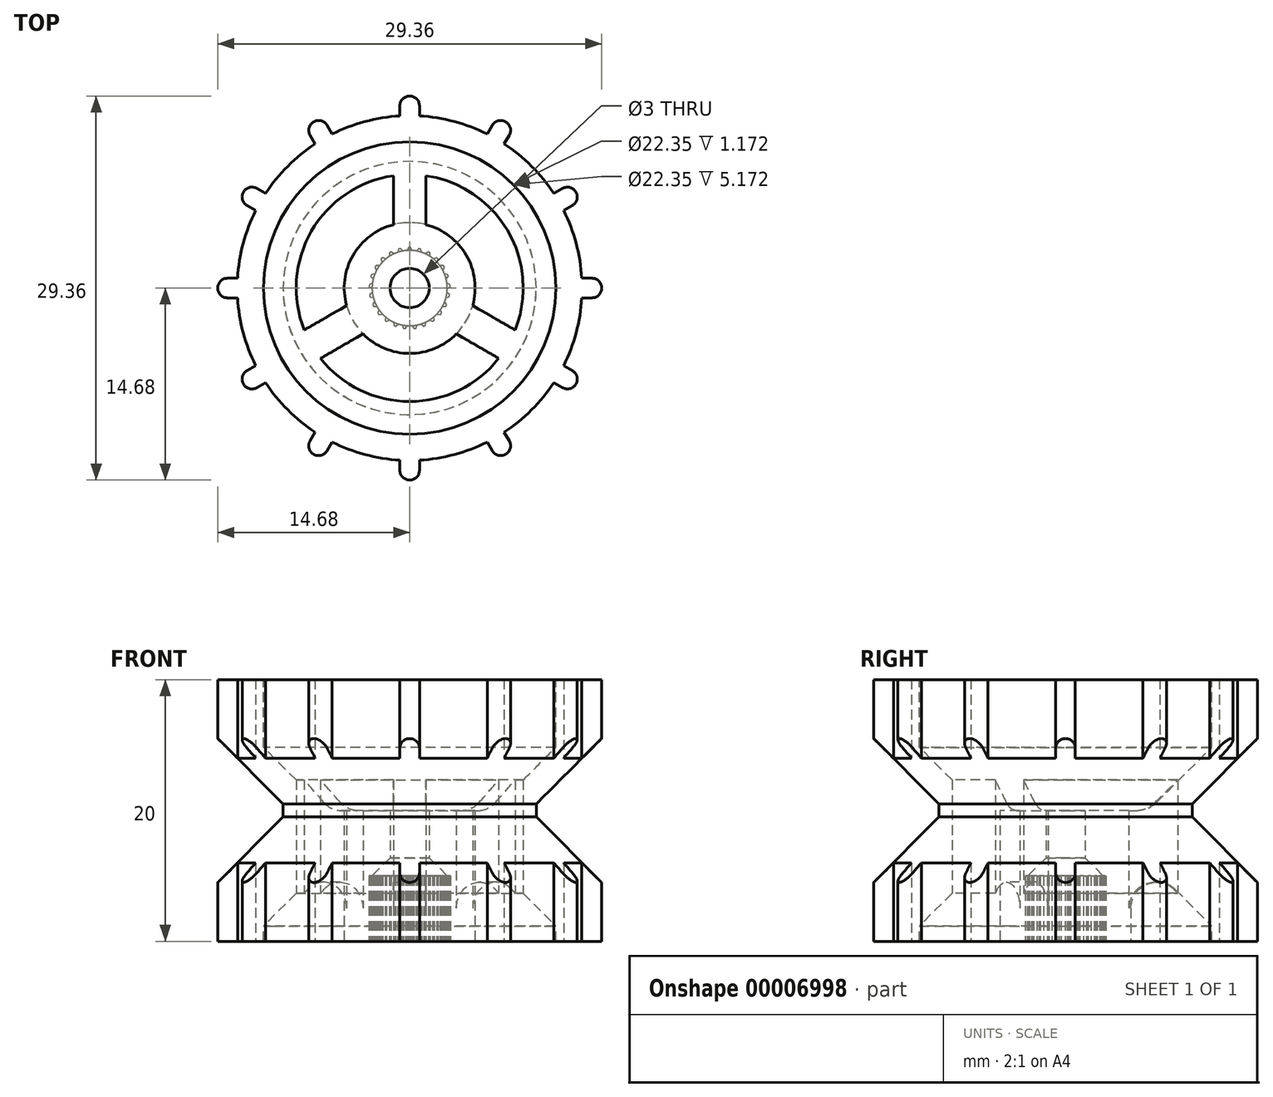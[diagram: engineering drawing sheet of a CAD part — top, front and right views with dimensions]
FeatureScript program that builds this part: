
annotation { "Feature Type Name" : "Feature", "Feature Type Description" : "" }
export const myFeature = defineFeature(function(context is Context, id is Id, definition is map)
    precondition{}
    {
        {
            var Q0;
            Q0=qCreatedBy(makeId("Top.planeOp"),FACE);
            var sketch = newSketch(context, id + "F0", { "sketchPlane" : qUnion([Q0])});
            skLineSegment(sketch, "E0.0", {"start": v(0.07, 3.1) * mm, "end": v(-0.08, 3.1) * mm});
            skLineSegment(sketch, "E0.1", {"start": v(0.25, 2.79) * mm, "end": v(0.07, 3.1) * mm});
            skArc(sketch, "E0.2", {"start": v(0.45, 2.76) * mm, "mid": v(0.35, 2.78) * mm, "end": v(0.25, 2.79) * mm});
            skLineSegment(sketch, "E1.1.0", {"start": v(-0.7, 3.02) * mm, "end": v(-0.84, 2.98) * mm});
            skLineSegment(sketch, "E1.1.1", {"start": v(-0.45, 2.76) * mm, "end": v(-0.7, 3.02) * mm});
            skArc(sketch, "E1.1.2", {"start": v(-0.25, 2.79) * mm, "mid": v(-0.35, 2.78) * mm, "end": v(-0.45, 2.76) * mm});
            skLineSegment(sketch, "E1.2.0", {"start": v(-1.43, 2.75) * mm, "end": v(-1.56, 2.68) * mm});
            skLineSegment(sketch, "E1.2.1", {"start": v(-1.12, 2.56) * mm, "end": v(-1.43, 2.75) * mm});
            skArc(sketch, "E1.2.2", {"start": v(-0.94, 2.64) * mm, "mid": v(-1.03, 2.6) * mm, "end": v(-1.12, 2.56) * mm});
            skLineSegment(sketch, "E1.3.0", {"start": v(-2.07, 2.31) * mm, "end": v(-2.18, 2.2) * mm});
            skLineSegment(sketch, "E1.3.1", {"start": v(-1.73, 2.2) * mm, "end": v(-2.07, 2.31) * mm});
            skArc(sketch, "E1.3.2", {"start": v(-1.56, 2.32) * mm, "mid": v(-1.65, 2.27) * mm, "end": v(-1.73, 2.2) * mm});
            skLineSegment(sketch, "E1.4.0", {"start": v(-2.58, 1.72) * mm, "end": v(-2.66, 1.6) * mm});
            skLineSegment(sketch, "E1.4.1", {"start": v(-2.22, 1.7) * mm, "end": v(-2.58, 1.72) * mm});
            skArc(sketch, "E1.4.2", {"start": v(-2.1, 1.86) * mm, "mid": v(-2.16, 1.78) * mm, "end": v(-2.22, 1.7) * mm});
            skLineSegment(sketch, "E1.5.0", {"start": v(-2.93, 1.03) * mm, "end": v(-2.97, 0.89) * mm});
            skLineSegment(sketch, "E1.5.1", {"start": v(-2.58, 1.1) * mm, "end": v(-2.93, 1.03) * mm});
            skArc(sketch, "E1.5.2", {"start": v(-2.49, 1.28) * mm, "mid": v(-2.53, 1.2) * mm, "end": v(-2.58, 1.1) * mm});
            skLineSegment(sketch, "E1.6.0", {"start": v(-3.09, 0.27) * mm, "end": v(-3.1, 0.12) * mm});
            skLineSegment(sketch, "E1.6.1", {"start": v(-2.77, 0.42) * mm, "end": v(-3.09, 0.27) * mm});
            skArc(sketch, "E1.6.2", {"start": v(-2.73, 0.62) * mm, "mid": v(-2.75, 0.52) * mm, "end": v(-2.77, 0.42) * mm});
            skLineSegment(sketch, "E1.7.0", {"start": v(-3.06, -0.5) * mm, "end": v(-3.03, -0.65) * mm});
            skLineSegment(sketch, "E1.7.1", {"start": v(-2.79, -0.28) * mm, "end": v(-3.06, -0.5) * mm});
            skArc(sketch, "E1.7.2", {"start": v(-2.8, -0.07) * mm, "mid": v(-2.8, -0.18) * mm, "end": v(-2.79, -0.28) * mm});
            skLineSegment(sketch, "E1.8.0", {"start": v(-2.84, -1.25) * mm, "end": v(-2.77, -1.39) * mm});
            skLineSegment(sketch, "E1.8.1", {"start": v(-2.63, -0.96) * mm, "end": v(-2.84, -1.25) * mm});
            skArc(sketch, "E1.8.2", {"start": v(-2.7, -0.77) * mm, "mid": v(-2.66, -0.87) * mm, "end": v(-2.63, -0.96) * mm});
            skLineSegment(sketch, "E1.9.0", {"start": v(-2.44, -1.92) * mm, "end": v(-2.34, -2.03) * mm});
            skLineSegment(sketch, "E1.9.1", {"start": v(-2.3, -1.59) * mm, "end": v(-2.44, -1.92) * mm});
            skArc(sketch, "E1.9.2", {"start": v(-2.42, -1.41) * mm, "mid": v(-2.36, -1.5) * mm, "end": v(-2.3, -1.59) * mm});
            skLineSegment(sketch, "E1.10.0", {"start": v(-1.88, -2.46) * mm, "end": v(-1.76, -2.55) * mm});
            skLineSegment(sketch, "E1.10.1", {"start": v(-1.84, -2.1) * mm, "end": v(-1.88, -2.46) * mm});
            skArc(sketch, "E1.10.2", {"start": v(-1.99, -1.97) * mm, "mid": v(-1.92, -2.04) * mm, "end": v(-1.84, -2.1) * mm});
            skLineSegment(sketch, "E1.11.0", {"start": v(-1.21, -2.85) * mm, "end": v(-1.07, -2.9) * mm});
            skLineSegment(sketch, "E1.11.1", {"start": v(-1.26, -2.5) * mm, "end": v(-1.21, -2.85) * mm});
            skArc(sketch, "E1.11.2", {"start": v(-1.44, -2.4) * mm, "mid": v(-1.35, -2.45) * mm, "end": v(-1.26, -2.5) * mm});
            skLineSegment(sketch, "E1.12.0", {"start": v(-0.46, -3.07) * mm, "end": v(-0.31, -3.08) * mm});
            skLineSegment(sketch, "E1.12.1", {"start": v(-0.6, -2.74) * mm, "end": v(-0.46, -3.07) * mm});
            skArc(sketch, "E1.12.2", {"start": v(-0.8, -2.69) * mm, "mid": v(-0.7, -2.71) * mm, "end": v(-0.6, -2.74) * mm});
            skLineSegment(sketch, "E1.13.0", {"start": v(0.31, -3.08) * mm, "end": v(0.46, -3.07) * mm});
            skLineSegment(sketch, "E1.13.1", {"start": v(0.1, -2.8) * mm, "end": v(0.31, -3.08) * mm});
            skArc(sketch, "E1.13.2", {"start": v(-0.1, -2.8) * mm, "mid": v(0, -2.8) * mm, "end": v(0.1, -2.8) * mm});
            skLineSegment(sketch, "E1.14.0", {"start": v(1.07, -2.9) * mm, "end": v(1.21, -2.85) * mm});
            skLineSegment(sketch, "E1.14.1", {"start": v(0.8, -2.69) * mm, "end": v(1.07, -2.9) * mm});
            skArc(sketch, "E1.14.2", {"start": v(0.6, -2.74) * mm, "mid": v(0.7, -2.71) * mm, "end": v(0.8, -2.69) * mm});
            skLineSegment(sketch, "E1.15.0", {"start": v(1.76, -2.55) * mm, "end": v(1.88, -2.46) * mm});
            skLineSegment(sketch, "E1.15.1", {"start": v(1.44, -2.4) * mm, "end": v(1.76, -2.55) * mm});
            skArc(sketch, "E1.15.2", {"start": v(1.26, -2.5) * mm, "mid": v(1.35, -2.45) * mm, "end": v(1.44, -2.4) * mm});
            skLineSegment(sketch, "E1.16.0", {"start": v(2.34, -2.03) * mm, "end": v(2.44, -1.92) * mm});
            skLineSegment(sketch, "E1.16.1", {"start": v(1.99, -1.97) * mm, "end": v(2.34, -2.03) * mm});
            skArc(sketch, "E1.16.2", {"start": v(1.84, -2.1) * mm, "mid": v(1.92, -2.04) * mm, "end": v(1.99, -1.97) * mm});
            skLineSegment(sketch, "E1.17.0", {"start": v(2.77, -1.39) * mm, "end": v(2.84, -1.25) * mm});
            skLineSegment(sketch, "E1.17.1", {"start": v(2.42, -1.41) * mm, "end": v(2.77, -1.39) * mm});
            skArc(sketch, "E1.17.2", {"start": v(2.3, -1.59) * mm, "mid": v(2.36, -1.5) * mm, "end": v(2.42, -1.41) * mm});
            skLineSegment(sketch, "E1.18.0", {"start": v(3.03, -0.65) * mm, "end": v(3.06, -0.5) * mm});
            skLineSegment(sketch, "E1.18.1", {"start": v(2.7, -0.77) * mm, "end": v(3.03, -0.65) * mm});
            skArc(sketch, "E1.18.2", {"start": v(2.63, -0.96) * mm, "mid": v(2.66, -0.87) * mm, "end": v(2.7, -0.77) * mm});
            skLineSegment(sketch, "E1.19.0", {"start": v(3.1, 0.12) * mm, "end": v(3.09, 0.27) * mm});
            skLineSegment(sketch, "E1.19.1", {"start": v(2.8, -0.07) * mm, "end": v(3.1, 0.12) * mm});
            skArc(sketch, "E1.19.2", {"start": v(2.79, -0.28) * mm, "mid": v(2.8, -0.18) * mm, "end": v(2.8, -0.07) * mm});
            skLineSegment(sketch, "E1.20.0", {"start": v(2.97, 0.89) * mm, "end": v(2.93, 1.03) * mm});
            skLineSegment(sketch, "E1.20.1", {"start": v(2.73, 0.62) * mm, "end": v(2.97, 0.89) * mm});
            skArc(sketch, "E1.20.2", {"start": v(2.77, 0.42) * mm, "mid": v(2.75, 0.52) * mm, "end": v(2.73, 0.62) * mm});
            skLineSegment(sketch, "E1.21.0", {"start": v(2.66, 1.6) * mm, "end": v(2.58, 1.72) * mm});
            skLineSegment(sketch, "E1.21.1", {"start": v(2.49, 1.28) * mm, "end": v(2.66, 1.6) * mm});
            skArc(sketch, "E1.21.2", {"start": v(2.58, 1.1) * mm, "mid": v(2.53, 1.2) * mm, "end": v(2.49, 1.28) * mm});
            skLineSegment(sketch, "E1.22.0", {"start": v(2.18, 2.2) * mm, "end": v(2.07, 2.31) * mm});
            skLineSegment(sketch, "E1.22.1", {"start": v(2.1, 1.86) * mm, "end": v(2.18, 2.2) * mm});
            skArc(sketch, "E1.22.2", {"start": v(2.22, 1.7) * mm, "mid": v(2.16, 1.78) * mm, "end": v(2.1, 1.86) * mm});
            skLineSegment(sketch, "E1.23.0", {"start": v(1.56, 2.68) * mm, "end": v(1.43, 2.75) * mm});
            skLineSegment(sketch, "E1.23.1", {"start": v(1.56, 2.32) * mm, "end": v(1.56, 2.68) * mm});
            skArc(sketch, "E1.23.2", {"start": v(1.73, 2.2) * mm, "mid": v(1.65, 2.27) * mm, "end": v(1.56, 2.32) * mm});
            skLineSegment(sketch, "E1.24.0", {"start": v(0.84, 2.98) * mm, "end": v(0.7, 3.02) * mm});
            skLineSegment(sketch, "E1.24.1", {"start": v(0.94, 2.64) * mm, "end": v(0.84, 2.98) * mm});
            skArc(sketch, "E1.24.2", {"start": v(1.12, 2.56) * mm, "mid": v(1.03, 2.6) * mm, "end": v(0.94, 2.64) * mm});
            skLineSegment(sketch, "E2", {"start": v(-0.08, 3.1) * mm, "end": v(-0.25, 2.79) * mm});
            skLineSegment(sketch, "E3.1.0", {"start": v(-0.84, 2.98) * mm, "end": v(-0.94, 2.64) * mm});
            skLineSegment(sketch, "E3.2.0", {"start": v(-1.56, 2.68) * mm, "end": v(-1.56, 2.32) * mm});
            skLineSegment(sketch, "E3.3.0", {"start": v(-2.18, 2.2) * mm, "end": v(-2.1, 1.86) * mm});
            skLineSegment(sketch, "E3.4.0", {"start": v(-2.66, 1.6) * mm, "end": v(-2.49, 1.28) * mm});
            skLineSegment(sketch, "E3.5.0", {"start": v(-2.97, 0.89) * mm, "end": v(-2.73, 0.62) * mm});
            skLineSegment(sketch, "E3.6.0", {"start": v(-3.1, 0.12) * mm, "end": v(-2.8, -0.07) * mm});
            skLineSegment(sketch, "E3.7.0", {"start": v(-3.03, -0.65) * mm, "end": v(-2.7, -0.77) * mm});
            skLineSegment(sketch, "E3.8.0", {"start": v(-2.77, -1.39) * mm, "end": v(-2.42, -1.41) * mm});
            skLineSegment(sketch, "E3.9.0", {"start": v(-2.34, -2.03) * mm, "end": v(-1.99, -1.97) * mm});
            skLineSegment(sketch, "E3.10.0", {"start": v(-1.76, -2.55) * mm, "end": v(-1.44, -2.4) * mm});
            skLineSegment(sketch, "E3.11.0", {"start": v(-1.07, -2.9) * mm, "end": v(-0.8, -2.69) * mm});
            skLineSegment(sketch, "E3.12.0", {"start": v(-0.31, -3.08) * mm, "end": v(-0.1, -2.8) * mm});
            skLineSegment(sketch, "E3.13.0", {"start": v(0.46, -3.07) * mm, "end": v(0.6, -2.74) * mm});
            skLineSegment(sketch, "E3.14.0", {"start": v(1.21, -2.85) * mm, "end": v(1.26, -2.5) * mm});
            skLineSegment(sketch, "E3.15.0", {"start": v(1.88, -2.46) * mm, "end": v(1.84, -2.1) * mm});
            skLineSegment(sketch, "E3.16.0", {"start": v(2.44, -1.92) * mm, "end": v(2.3, -1.59) * mm});
            skLineSegment(sketch, "E3.17.0", {"start": v(2.84, -1.25) * mm, "end": v(2.63, -0.96) * mm});
            skLineSegment(sketch, "E3.18.0", {"start": v(3.06, -0.5) * mm, "end": v(2.79, -0.28) * mm});
            skLineSegment(sketch, "E3.19.0", {"start": v(3.09, 0.27) * mm, "end": v(2.77, 0.42) * mm});
            skLineSegment(sketch, "E3.20.0", {"start": v(2.93, 1.03) * mm, "end": v(2.58, 1.1) * mm});
            skLineSegment(sketch, "E3.21.0", {"start": v(2.58, 1.72) * mm, "end": v(2.22, 1.7) * mm});
            skLineSegment(sketch, "E3.22.0", {"start": v(2.07, 2.31) * mm, "end": v(1.73, 2.2) * mm});
            skLineSegment(sketch, "E3.23.0", {"start": v(1.43, 2.75) * mm, "end": v(1.12, 2.56) * mm});
            skLineSegment(sketch, "E3.24.0", {"start": v(0.7, 3.02) * mm, "end": v(0.45, 2.76) * mm});
            skSolve(sketch);
        }
        {
            var Q0;
            Q0=qCreatedBy(makeId("Top.planeOp"),FACE);
            var sketch = newSketch(context, id + "F1", { "sketchPlane" : qUnion([Q0])});
            skArc(sketch, "E4", {"start": v(-0.75, 13.15) * mm, "mid": v(-3.4, 12.73) * mm, "end": v(-5.93, 11.77) * mm});
            skArc(sketch, "E5", {"start": v(0.75, 13.93) * mm, "mid": v(0, 14.68) * mm, "end": v(-0.75, 13.93) * mm});
            skLineSegment(sketch, "E6", {"start": v(-0.75, 13.93) * mm, "end": v(-0.75, 13.15) * mm});
            skLineSegment(sketch, "E7", {"start": v(0.75, 13.93) * mm, "end": v(0.75, 13.15) * mm});
            skPoint(sketch, "E8.end.orphan", {"position": v(0, 14.68) * mm});
            skPoint(sketch, "E9.1.0", {"position": v(-7.34, 12.7) * mm});
            skArc(sketch, "E9.1.1", {"start": v(-6.31, 12.43) * mm, "mid": v(-7.34, 12.7) * mm, "end": v(-7.61, 11.68) * mm});
            skLineSegment(sketch, "E9.1.2", {"start": v(-6.31, 12.43) * mm, "end": v(-5.93, 11.77) * mm});
            skLineSegment(sketch, "E9.1.3", {"start": v(-7.61, 11.68) * mm, "end": v(-7.23, 11.02) * mm});
            skPoint(sketch, "E9.2.0", {"position": v(-12.7, 7.34) * mm});
            skArc(sketch, "E9.2.1", {"start": v(-11.68, 7.61) * mm, "mid": v(-12.7, 7.34) * mm, "end": v(-12.43, 6.31) * mm});
            skLineSegment(sketch, "E9.2.2", {"start": v(-11.68, 7.61) * mm, "end": v(-11.02, 7.23) * mm});
            skLineSegment(sketch, "E9.2.3", {"start": v(-12.43, 6.31) * mm, "end": v(-11.77, 5.93) * mm});
            skPoint(sketch, "E9.3.0", {"position": v(-14.68, 0) * mm});
            skArc(sketch, "E9.3.1", {"start": v(-13.93, 0.75) * mm, "mid": v(-14.68, 0) * mm, "end": v(-13.93, -0.75) * mm});
            skLineSegment(sketch, "E9.3.2", {"start": v(-13.93, 0.75) * mm, "end": v(-13.15, 0.75) * mm});
            skLineSegment(sketch, "E9.3.3", {"start": v(-13.93, -0.75) * mm, "end": v(-13.15, -0.75) * mm});
            skPoint(sketch, "E9.4.0", {"position": v(-12.7, -7.34) * mm});
            skArc(sketch, "E9.4.1", {"start": v(-12.43, -6.31) * mm, "mid": v(-12.7, -7.34) * mm, "end": v(-11.68, -7.61) * mm});
            skLineSegment(sketch, "E9.4.2", {"start": v(-12.43, -6.31) * mm, "end": v(-11.77, -5.93) * mm});
            skLineSegment(sketch, "E9.4.3", {"start": v(-11.68, -7.61) * mm, "end": v(-11.02, -7.23) * mm});
            skPoint(sketch, "E9.5.0", {"position": v(-7.34, -12.7) * mm});
            skArc(sketch, "E9.5.1", {"start": v(-7.61, -11.68) * mm, "mid": v(-7.34, -12.7) * mm, "end": v(-6.31, -12.43) * mm});
            skLineSegment(sketch, "E9.5.2", {"start": v(-7.61, -11.68) * mm, "end": v(-7.23, -11.02) * mm});
            skLineSegment(sketch, "E9.5.3", {"start": v(-6.31, -12.43) * mm, "end": v(-5.93, -11.77) * mm});
            skPoint(sketch, "E9.6.0", {"position": v(0, -14.68) * mm});
            skArc(sketch, "E9.6.1", {"start": v(-0.75, -13.93) * mm, "mid": v(0, -14.68) * mm, "end": v(0.75, -13.93) * mm});
            skLineSegment(sketch, "E9.6.2", {"start": v(-0.75, -13.93) * mm, "end": v(-0.75, -13.15) * mm});
            skLineSegment(sketch, "E9.6.3", {"start": v(0.75, -13.93) * mm, "end": v(0.75, -13.15) * mm});
            skPoint(sketch, "E9.7.0", {"position": v(7.34, -12.7) * mm});
            skArc(sketch, "E9.7.1", {"start": v(6.31, -12.43) * mm, "mid": v(7.34, -12.7) * mm, "end": v(7.61, -11.68) * mm});
            skLineSegment(sketch, "E9.7.2", {"start": v(6.31, -12.43) * mm, "end": v(5.93, -11.77) * mm});
            skLineSegment(sketch, "E9.7.3", {"start": v(7.61, -11.68) * mm, "end": v(7.23, -11.02) * mm});
            skPoint(sketch, "E9.8.0", {"position": v(12.7, -7.34) * mm});
            skArc(sketch, "E9.8.1", {"start": v(11.68, -7.61) * mm, "mid": v(12.7, -7.34) * mm, "end": v(12.43, -6.31) * mm});
            skLineSegment(sketch, "E9.8.2", {"start": v(11.68, -7.61) * mm, "end": v(11.02, -7.23) * mm});
            skLineSegment(sketch, "E9.8.3", {"start": v(12.43, -6.31) * mm, "end": v(11.77, -5.93) * mm});
            skPoint(sketch, "E9.9.0", {"position": v(14.68, 0) * mm});
            skArc(sketch, "E9.9.1", {"start": v(13.93, -0.75) * mm, "mid": v(14.68, 0) * mm, "end": v(13.93, 0.75) * mm});
            skLineSegment(sketch, "E9.9.2", {"start": v(13.93, -0.75) * mm, "end": v(13.15, -0.75) * mm});
            skLineSegment(sketch, "E9.9.3", {"start": v(13.93, 0.75) * mm, "end": v(13.15, 0.75) * mm});
            skPoint(sketch, "E9.10.0", {"position": v(12.7, 7.34) * mm});
            skArc(sketch, "E9.10.1", {"start": v(12.43, 6.31) * mm, "mid": v(12.7, 7.34) * mm, "end": v(11.68, 7.61) * mm});
            skLineSegment(sketch, "E9.10.2", {"start": v(12.43, 6.31) * mm, "end": v(11.77, 5.93) * mm});
            skLineSegment(sketch, "E9.10.3", {"start": v(11.68, 7.61) * mm, "end": v(11.02, 7.23) * mm});
            skPoint(sketch, "E9.11.0", {"position": v(7.34, 12.7) * mm});
            skArc(sketch, "E9.11.1", {"start": v(7.61, 11.68) * mm, "mid": v(7.34, 12.7) * mm, "end": v(6.31, 12.43) * mm});
            skLineSegment(sketch, "E9.11.2", {"start": v(7.61, 11.68) * mm, "end": v(7.23, 11.02) * mm});
            skLineSegment(sketch, "E9.11.3", {"start": v(6.31, 12.43) * mm, "end": v(5.93, 11.77) * mm});
            skArc(sketch, "E10.trimOffspring", {"start": v(-7.23, 11.02) * mm, "mid": v(-9.32, 9.32) * mm, "end": v(-11.02, 7.23) * mm});
            skArc(sketch, "E11.trimOffspring", {"start": v(-11.77, 5.93) * mm, "mid": v(-12.73, 3.4) * mm, "end": v(-13.15, 0.75) * mm});
            skArc(sketch, "E12.trimOffspring", {"start": v(-13.15, -0.75) * mm, "mid": v(-12.73, -3.4) * mm, "end": v(-11.77, -5.93) * mm});
            skArc(sketch, "E13.trimOffspring", {"start": v(-11.02, -7.23) * mm, "mid": v(-9.32, -9.32) * mm, "end": v(-7.23, -11.02) * mm});
            skArc(sketch, "E14.trimOffspring", {"start": v(5.93, 11.77) * mm, "mid": v(3.4, 12.73) * mm, "end": v(0.75, 13.15) * mm});
            skArc(sketch, "E15.trimOffspring", {"start": v(11.02, 7.23) * mm, "mid": v(9.32, 9.32) * mm, "end": v(7.23, 11.02) * mm});
            skArc(sketch, "E16.trimOffspring", {"start": v(13.15, 0.75) * mm, "mid": v(12.73, 3.4) * mm, "end": v(11.77, 5.93) * mm});
            skArc(sketch, "E17.trimOffspring", {"start": v(11.77, -5.93) * mm, "mid": v(12.73, -3.4) * mm, "end": v(13.15, -0.75) * mm});
            skArc(sketch, "E18.trimOffspring", {"start": v(7.23, -11.02) * mm, "mid": v(9.32, -9.32) * mm, "end": v(11.02, -7.23) * mm});
            skArc(sketch, "E19.trimOffspring", {"start": v(0.75, -13.15) * mm, "mid": v(3.4, -12.73) * mm, "end": v(5.93, -11.77) * mm});
            skArc(sketch, "E20.trimOffspring", {"start": v(-5.93, -11.77) * mm, "mid": v(-3.4, -12.73) * mm, "end": v(-0.75, -13.15) * mm});
            skCircle(sketch, "E21", {"center": v(0, 0) * mm, "radius": 1.5 * mm});
            skLineSegment(sketch, "E22", {"start": v(1.25, 4.84) * mm, "end": v(1.25, 8.58) * mm});
            skLineSegment(sketch, "E23", {"start": v(-1.25, 4.84) * mm, "end": v(-1.25, 8.58) * mm});
            skArc(sketch, "E24", {"start": v(4.82, -1.34) * mm, "mid": v(4.33, 2.5) * mm, "end": v(1.25, 4.84) * mm});
            skLineSegment(sketch, "E25.1.0", {"start": v(-3.57, -3.5) * mm, "end": v(-6.8, -5.37) * mm});
            skLineSegment(sketch, "E25.1.1", {"start": v(-4.82, -1.34) * mm, "end": v(-8.06, -3.2) * mm});
            skLineSegment(sketch, "E25.2.0", {"start": v(4.82, -1.34) * mm, "end": v(8.06, -3.2) * mm});
            skLineSegment(sketch, "E25.2.1", {"start": v(3.57, -3.5) * mm, "end": v(6.8, -5.37) * mm});
            skArc(sketch, "E26.trimOffspring", {"start": v(-3.57, -3.5) * mm, "mid": v(0, -5) * mm, "end": v(3.57, -3.5) * mm});
            skArc(sketch, "E27.trimOffspring", {"start": v(-1.25, 4.84) * mm, "mid": v(-4.33, 2.5) * mm, "end": v(-4.82, -1.34) * mm});
            skArc(sketch, "E28", {"start": v(8.06, -3.2) * mm, "mid": v(7.51, 4.34) * mm, "end": v(1.25, 8.58) * mm});
            skPoint(sketch, "E29.orphan", {"position": v(9.15, -3.84) * mm});
            skPoint(sketch, "E30.orphan", {"position": v(7.9, -6) * mm});
            skPoint(sketch, "E31.orphan", {"position": v(-7.9, -6) * mm});
            skArc(sketch, "E32.trimOffspring", {"start": v(-6.8, -5.37) * mm, "mid": v(0, -8.68) * mm, "end": v(6.8, -5.37) * mm});
            skPoint(sketch, "E33.orphan", {"position": v(-9.15, -3.84) * mm});
            skPoint(sketch, "E34.orphan", {"position": v(-1.25, 9.85) * mm});
            skArc(sketch, "E35.trimOffspring", {"start": v(-1.25, 8.58) * mm, "mid": v(-7.51, 4.34) * mm, "end": v(-8.06, -3.2) * mm});
            skPoint(sketch, "E36.orphan", {"position": v(1.25, 9.85) * mm});
            skSolve(sketch);
        }
        {
            var Q0;
            Q0=qCreatedBy(makeId("Front.planeOp"),FACE);
            var sketch = newSketch(context, id + "F2", { "sketchPlane" : qUnion([Q0])});
            skLineSegment(sketch, "E37", {"start": v(0, 0) * mm, "end": v(0, 27.05) * mm, "construction": true});
            skSolve(sketch);
        }
        {
            var Q0;
            Q0 = qSketchRegion(id + "F1", true);
            extrude(context, id + "F3", {"entities" : qUnion([Q0]), "depth" : 20 * mm});
        }
        {
            var Q0;
            Q0=qCreatedBy(makeId("Front.planeOp"),FACE);
            var sketch = newSketch(context, id + "F4", { "sketchPlane" : qUnion([Q0])});
            skLineSegment(sketch, "E38", {"start": v(0, 20) * mm, "end": v(0, 10) * mm});
            skLineSegment(sketch, "E39", {"start": v(13.18, 14) * mm, "end": v(9.67, 10.5) * mm});
            skLineSegment(sketch, "E40", {"start": v(9.68, 10) * mm, "end": v(9.68, 10.5) * mm});
            skLineSegment(sketch, "E41", {"start": v(9.68, 10) * mm, "end": v(9.68, 9.5) * mm});
            skLineSegment(sketch, "E42", {"start": v(9.68, 9.5) * mm, "end": v(13.18, 6) * mm});
            skLineSegment(sketch, "E43", {"start": v(13.18, 14) * mm, "end": v(15.36, 16.19) * mm});
            skLineSegment(sketch, "E44", {"start": v(15.36, 16.19) * mm, "end": v(15.36, 3.81) * mm});
            skLineSegment(sketch, "E45", {"start": v(13.18, 6) * mm, "end": v(15.36, 3.81) * mm});
            skLineSegment(sketch, "E46", {"start": v(0, 10) * mm, "end": v(6.35, 10) * mm});
            skLineSegment(sketch, "E47", {"start": v(0, 20) * mm, "end": v(11.18, 20) * mm});
            skLineSegment(sketch, "E48", {"start": v(11.18, 20) * mm, "end": v(11.18, 14.83) * mm});
            skLineSegment(sketch, "E49", {"start": v(6.35, 10) * mm, "end": v(11.17, 14.83) * mm});
            skLineSegment(sketch, "E50", {"start": v(11.18, 1.17) * mm, "end": v(11.18, 0) * mm});
            skLineSegment(sketch, "E51", {"start": v(0, 0) * mm, "end": v(5, 0) * mm});
            skLineSegment(sketch, "E52", {"start": v(5, 0) * mm, "end": v(5, 7.35) * mm});
            skLineSegment(sketch, "E53", {"start": v(11.18, 0) * mm, "end": v(5, 0) * mm});
            skLineSegment(sketch, "E54", {"start": v(5, 7.35) * mm, "end": v(11.18, 1.17) * mm});
            skSolve(sketch);
        }
        {
            var Q0;
            Q0 = qSketchRegion(id + "F4", true);
            var Q1;
            Q1=sQuery(id+"F2.wireOp",EDGE,"E37");
            revolve(context, id + "F5", {"operationType" : NewBodyOperationType.REMOVE, "entities" : qUnion([Q0]), "axis" : qUnion([Q1]), "revolveType" : RevolveType.FULL, "oppositeDirection" : true});
        }
        {
            var Q0;
            Q0=makeQuery(id+"F5.boolean.opBoolean","COPY",EDGE,{"disambiguationData":[OD(1.0)],"derivedFrom":makeQuery(id+"F5.opRevolve","SWEPT_EDGE",EDGE,{"disambiguationData":[OSD([sQuery(id+"F4.wireOp",EDGE,"E46"),sQuery(id+"F4.wireOp",EDGE,"E49")])]})});
            var Q1;
            Q1=makeQuery(id+"F5.boolean.opBoolean","COPY",EDGE,{"disambiguationData":[OD(0.0)],"derivedFrom":makeQuery(id+"F5.opRevolve","SWEPT_EDGE",EDGE,{"disambiguationData":[OSD([sQuery(id+"F4.wireOp",EDGE,"E46"),sQuery(id+"F4.wireOp",EDGE,"E49")])]})});
            var Q2;
            Q2=makeQuery(id+"F5.boolean.opBoolean","COPY",EDGE,{"disambiguationData":[OD(2.0)],"derivedFrom":makeQuery(id+"F5.opRevolve","SWEPT_EDGE",EDGE,{"disambiguationData":[OSD([sQuery(id+"F4.wireOp",EDGE,"E46"),sQuery(id+"F4.wireOp",EDGE,"E49")])]})});
            fillet(context, id + "F6", {"entities" : qUnion([Q0, Q1, Q2]), "radius" : 2 * mm, "tangentPropagation" : true, "allowEdgeOverflow" : false});
        }
        {
            var Q0;
            Q0=makeQuery(id+"F5.boolean.opBoolean","COPY",EDGE,{"disambiguationData":[OD(0.0)],"derivedFrom":makeQuery(id+"F5.opRevolve","SWEPT_EDGE",EDGE,{"disambiguationData":[OSD([sQuery(id+"F4.wireOp",EDGE,"E52"),sQuery(id+"F4.wireOp",EDGE,"E54")])]})});
            var Q1;
            Q1=makeQuery(id+"F5.boolean.opBoolean","COPY",EDGE,{"disambiguationData":[OD(2.0)],"derivedFrom":makeQuery(id+"F5.opRevolve","SWEPT_EDGE",EDGE,{"disambiguationData":[OSD([sQuery(id+"F4.wireOp",EDGE,"E52"),sQuery(id+"F4.wireOp",EDGE,"E54")])]})});
            var Q2;
            Q2=makeQuery(id+"F5.boolean.opBoolean","COPY",EDGE,{"disambiguationData":[OD(1.0)],"derivedFrom":makeQuery(id+"F5.opRevolve","SWEPT_EDGE",EDGE,{"disambiguationData":[OSD([sQuery(id+"F4.wireOp",EDGE,"E52"),sQuery(id+"F4.wireOp",EDGE,"E54")])]})});
            fillet(context, id + "F7", {"entities" : qUnion([Q0, Q1, Q2]), "radius" : 2 * mm, "tangentPropagation" : true, "allowEdgeOverflow" : false});
        }
        {
            var Q0;
            Q0 = qSketchRegion(id + "F0", true);
            extrude(context, id + "F8", {"entities" : qUnion([Q0]), "operationType" : NewBodyOperationType.REMOVE, "depth" : 5 * mm});
        }
        {
            var Q0;
            Q0=qCreatedBy(makeId("Top.planeOp"),FACE);
            var sketch = newSketch(context, id + "F9", { "sketchPlane" : qUnion([Q0])});
            skCircle(sketch, "E55", {"center": v(0, 0) * mm, "radius": 2.87 * mm});
            skSolve(sketch);
        }
        {
            var Q0;
            Q0 = qSketchRegion(id + "F9", true);
            extrude(context, id + "F10", {"entities" : qUnion([Q0]), "operationType" : NewBodyOperationType.REMOVE, "depth" : 5 * mm});
        }
        {
            var Q0;
            Q0=makeQuery(id+"F8.boolean.opBoolean","INTERSECT",EDGE,{"derivedFrom":[makeQuery(id+"F3.opExtrude","SWEPT_FACE",FACE,{"disambiguationData":[OSD([sQuery(id+"F1.wireOp",EDGE,"E21")])]}),makeQuery(id+"F8.opExtrude","CAP_FACE",FACE,{"disambiguationData":[OSD([sQuery(id+"F0.wireOp",EDGE,"E0.0"),sQuery(id+"F0.wireOp",EDGE,"E0.1"),sQuery(id+"F0.wireOp",EDGE,"E0.2"),sQuery(id+"F0.wireOp",EDGE,"E1.1.0"),sQuery(id+"F0.wireOp",EDGE,"E1.1.1"),sQuery(id+"F0.wireOp",EDGE,"E1.1.2"),sQuery(id+"F0.wireOp",EDGE,"E1.2.0"),sQuery(id+"F0.wireOp",EDGE,"E1.2.1"),sQuery(id+"F0.wireOp",EDGE,"E1.2.2"),sQuery(id+"F0.wireOp",EDGE,"E1.3.0"),sQuery(id+"F0.wireOp",EDGE,"E1.3.1"),sQuery(id+"F0.wireOp",EDGE,"E1.3.2"),sQuery(id+"F0.wireOp",EDGE,"E1.4.0"),sQuery(id+"F0.wireOp",EDGE,"E1.4.1"),sQuery(id+"F0.wireOp",EDGE,"E1.4.2"),sQuery(id+"F0.wireOp",EDGE,"E1.5.0"),sQuery(id+"F0.wireOp",EDGE,"E1.5.1"),sQuery(id+"F0.wireOp",EDGE,"E1.5.2"),sQuery(id+"F0.wireOp",EDGE,"E1.6.0"),sQuery(id+"F0.wireOp",EDGE,"E1.6.1"),sQuery(id+"F0.wireOp",EDGE,"E1.6.2"),sQuery(id+"F0.wireOp",EDGE,"E1.7.0"),sQuery(id+"F0.wireOp",EDGE,"E1.7.1"),sQuery(id+"F0.wireOp",EDGE,"E1.7.2"),sQuery(id+"F0.wireOp",EDGE,"E1.8.0"),sQuery(id+"F0.wireOp",EDGE,"E1.8.1"),sQuery(id+"F0.wireOp",EDGE,"E1.8.2"),sQuery(id+"F0.wireOp",EDGE,"E1.9.0"),sQuery(id+"F0.wireOp",EDGE,"E1.9.1"),sQuery(id+"F0.wireOp",EDGE,"E1.9.2"),sQuery(id+"F0.wireOp",EDGE,"E1.10.0"),sQuery(id+"F0.wireOp",EDGE,"E1.10.1"),sQuery(id+"F0.wireOp",EDGE,"E1.10.2"),sQuery(id+"F0.wireOp",EDGE,"E1.11.0"),sQuery(id+"F0.wireOp",EDGE,"E1.11.1"),sQuery(id+"F0.wireOp",EDGE,"E1.11.2"),sQuery(id+"F0.wireOp",EDGE,"E1.12.0"),sQuery(id+"F0.wireOp",EDGE,"E1.12.1"),sQuery(id+"F0.wireOp",EDGE,"E1.12.2"),sQuery(id+"F0.wireOp",EDGE,"E1.13.0"),sQuery(id+"F0.wireOp",EDGE,"E1.13.1"),sQuery(id+"F0.wireOp",EDGE,"E1.13.2"),sQuery(id+"F0.wireOp",EDGE,"E1.14.0"),sQuery(id+"F0.wireOp",EDGE,"E1.14.1"),sQuery(id+"F0.wireOp",EDGE,"E1.14.2"),sQuery(id+"F0.wireOp",EDGE,"E1.15.0"),sQuery(id+"F0.wireOp",EDGE,"E1.15.1"),sQuery(id+"F0.wireOp",EDGE,"E1.15.2"),sQuery(id+"F0.wireOp",EDGE,"E1.16.0"),sQuery(id+"F0.wireOp",EDGE,"E1.16.1"),sQuery(id+"F0.wireOp",EDGE,"E1.16.2"),sQuery(id+"F0.wireOp",EDGE,"E1.17.0"),sQuery(id+"F0.wireOp",EDGE,"E1.17.1"),sQuery(id+"F0.wireOp",EDGE,"E1.17.2"),sQuery(id+"F0.wireOp",EDGE,"E1.18.0"),sQuery(id+"F0.wireOp",EDGE,"E1.18.1"),sQuery(id+"F0.wireOp",EDGE,"E1.18.2"),sQuery(id+"F0.wireOp",EDGE,"E1.19.0"),sQuery(id+"F0.wireOp",EDGE,"E1.19.1"),sQuery(id+"F0.wireOp",EDGE,"E1.19.2"),sQuery(id+"F0.wireOp",EDGE,"E1.20.0"),sQuery(id+"F0.wireOp",EDGE,"E1.20.1"),sQuery(id+"F0.wireOp",EDGE,"E1.20.2"),sQuery(id+"F0.wireOp",EDGE,"E1.21.0"),sQuery(id+"F0.wireOp",EDGE,"E1.21.1"),sQuery(id+"F0.wireOp",EDGE,"E1.21.2"),sQuery(id+"F0.wireOp",EDGE,"E1.22.0"),sQuery(id+"F0.wireOp",EDGE,"E1.22.1"),sQuery(id+"F0.wireOp",EDGE,"E1.22.2"),sQuery(id+"F0.wireOp",EDGE,"E1.23.0"),sQuery(id+"F0.wireOp",EDGE,"E1.23.1"),sQuery(id+"F0.wireOp",EDGE,"E1.23.2"),sQuery(id+"F0.wireOp",EDGE,"E1.24.0"),sQuery(id+"F0.wireOp",EDGE,"E1.24.1"),sQuery(id+"F0.wireOp",EDGE,"E1.24.2"),sQuery(id+"F0.wireOp",EDGE,"E2"),sQuery(id+"F0.wireOp",EDGE,"E3.1.0"),sQuery(id+"F0.wireOp",EDGE,"E3.2.0"),sQuery(id+"F0.wireOp",EDGE,"E3.3.0"),sQuery(id+"F0.wireOp",EDGE,"E3.4.0"),sQuery(id+"F0.wireOp",EDGE,"E3.5.0"),sQuery(id+"F0.wireOp",EDGE,"E3.6.0"),sQuery(id+"F0.wireOp",EDGE,"E3.7.0"),sQuery(id+"F0.wireOp",EDGE,"E3.8.0"),sQuery(id+"F0.wireOp",EDGE,"E3.9.0"),sQuery(id+"F0.wireOp",EDGE,"E3.10.0"),sQuery(id+"F0.wireOp",EDGE,"E3.11.0"),sQuery(id+"F0.wireOp",EDGE,"E3.12.0"),sQuery(id+"F0.wireOp",EDGE,"E3.13.0"),sQuery(id+"F0.wireOp",EDGE,"E3.14.0"),sQuery(id+"F0.wireOp",EDGE,"E3.15.0"),sQuery(id+"F0.wireOp",EDGE,"E3.16.0"),sQuery(id+"F0.wireOp",EDGE,"E3.17.0"),sQuery(id+"F0.wireOp",EDGE,"E3.18.0"),sQuery(id+"F0.wireOp",EDGE,"E3.19.0"),sQuery(id+"F0.wireOp",EDGE,"E3.20.0"),sQuery(id+"F0.wireOp",EDGE,"E3.21.0"),sQuery(id+"F0.wireOp",EDGE,"E3.22.0"),sQuery(id+"F0.wireOp",EDGE,"E3.23.0"),sQuery(id+"F0.wireOp",EDGE,"E3.24.0")])],"isStart":false})]});
            chamfer(context, id + "F11", {"entities" : qUnion([Q0]), "width" : 1.38 * mm, "tangentPropagation" : true});
        }
    });
